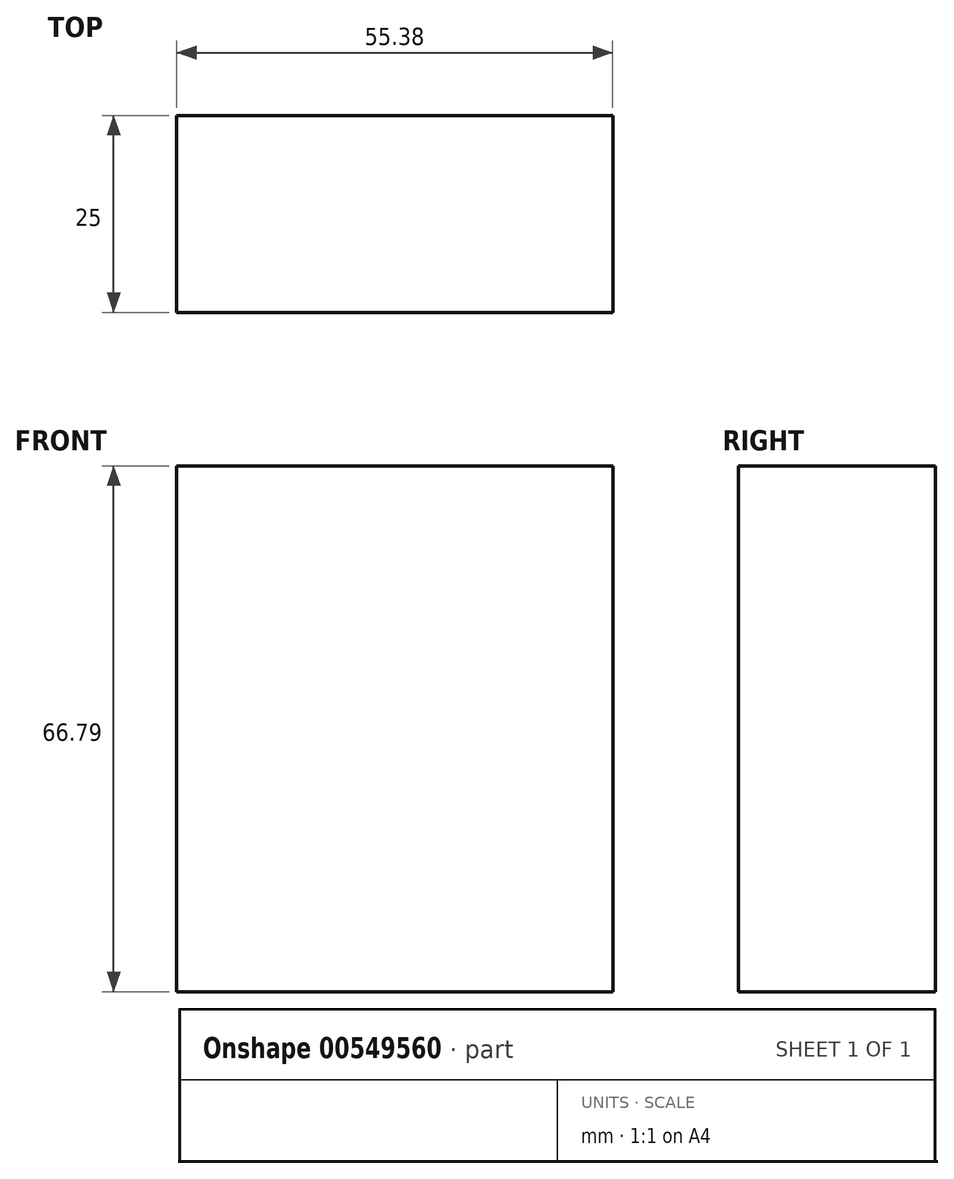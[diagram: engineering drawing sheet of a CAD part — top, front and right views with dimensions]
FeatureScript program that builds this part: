
annotation { "Feature Type Name" : "Feature", "Feature Type Description" : "" }
export const myFeature = defineFeature(function(context is Context, id is Id, definition is map)
    precondition{}
    {
        {
            var Q0;
            Q0=qCreatedBy(makeId("Front.planeOp"),FACE);
            var sketch = newSketch(context, id + "F0", { "sketchPlane" : qUnion([Q0])});
            skLineSegment(sketch, "E0.bottom", {"start": v(-132.3, 49.96) * mm, "end": v(-76.92, 49.96) * mm});
            skLineSegment(sketch, "E0.top", {"start": v(-132.3, -16.83) * mm, "end": v(-76.92, -16.83) * mm});
            skLineSegment(sketch, "E0.left", {"start": v(-132.3, 49.96) * mm, "end": v(-132.3, -16.83) * mm});
            skLineSegment(sketch, "E0.right", {"start": v(-76.92, 49.96) * mm, "end": v(-76.92, -16.83) * mm});
            skSolve(sketch);
        }
        {
            var Q0;
            Q0 = qSketchRegion(id + "F0", true);
            extrude(context, id + "F1", {"entities" : qUnion([Q0]), "depth" : 25 * mm, "offsetDistance" : 25 * mm});
        }
    });
